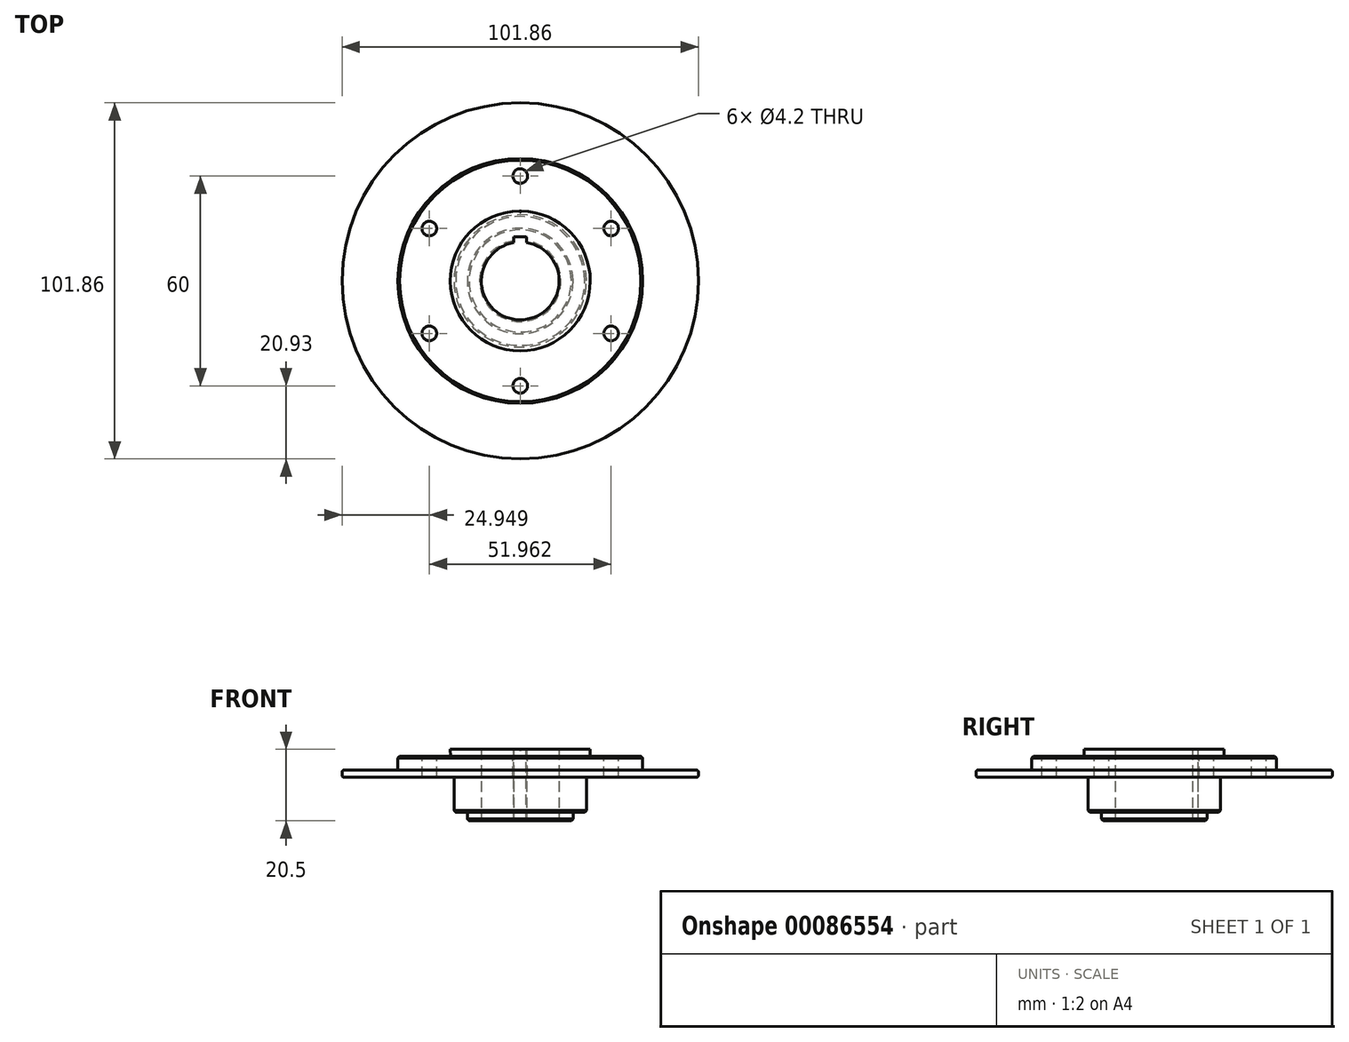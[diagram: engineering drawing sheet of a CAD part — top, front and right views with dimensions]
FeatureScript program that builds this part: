
annotation { "Feature Type Name" : "Feature", "Feature Type Description" : "" }
export const myFeature = defineFeature(function(context is Context, id is Id, definition is map)
    precondition{}
    {
        {
            var Q0;
            Q0=qCreatedBy(makeId("Front.planeOp"),FACE);
            var sketch = newSketch(context, id + "F0", { "sketchPlane" : qUnion([Q0])});
            skLineSegment(sketch, "E0", {"start": v(-11.12, -17.6) * mm, "end": v(-15.1, -17.6) * mm});
            skLineSegment(sketch, "E1", {"start": v(-15.1, -17.6) * mm, "end": v(-15.1, -15.1) * mm});
            skLineSegment(sketch, "E2", {"start": v(-15.1, -15.1) * mm, "end": v(-18.93, -15.1) * mm});
            skLineSegment(sketch, "E3", {"start": v(-18.93, -15.1) * mm, "end": v(-18.93, -5.1) * mm});
            skLineSegment(sketch, "E4", {"start": v(0, 0) * mm, "end": v(0, 28.12) * mm, "construction": true});
            skLineSegment(sketch, "E5", {"start": v(-11.12, -17.6) * mm, "end": v(-11.12, 8.2) * mm, "construction": true});
            skLineSegment(sketch, "E6", {"start": v(-35, 0.9) * mm, "end": v(-19.97, 0.9) * mm});
            skLineSegment(sketch, "E7", {"start": v(-35, 0.9) * mm, "end": v(-35, -3.1) * mm});
            skLineSegment(sketch, "E8", {"start": v(-11.12, -17.6) * mm, "end": v(-11.12, 2.9) * mm});
            skLineSegment(sketch, "E9", {"start": v(-11.13, 2.9) * mm, "end": v(-20, 2.9) * mm});
            skLineSegment(sketch, "E10", {"start": v(-20, 2.9) * mm, "end": v(-19.97, 0.9) * mm});
            skLineSegment(sketch, "E11", {"start": v(-35, -3.1) * mm, "end": v(-50.43, -3.1) * mm});
            skLineSegment(sketch, "E12", {"start": v(-50.93, -3.6) * mm, "end": v(-50.93, -4.6) * mm});
            skLineSegment(sketch, "E13", {"start": v(-50.43, -5.1) * mm, "end": v(-18.93, -5.1) * mm});
            skPoint(sketch, "E14.visualSharp", {"position": v(-50.93, -3.1) * mm});
            skArc(sketch, "E14.filletArc", {"start": v(-50.43, -3.1) * mm, "mid": v(-50.78, -3.25) * mm, "end": v(-50.93, -3.6) * mm});
            skPoint(sketch, "E15.visualSharp", {"position": v(-50.93, -5.1) * mm});
            skArc(sketch, "E15.filletArc", {"start": v(-50.93, -4.6) * mm, "mid": v(-50.78, -4.95) * mm, "end": v(-50.43, -5.1) * mm});
            skSolve(sketch);
        }
        {
            var Q0;
            Q0=makeQuery(id+"F0.imprint","IMPRINT",FACE,{"disambiguationData":[TD([[makeQuery(id+"F0.imprint","IMPRINT",EDGE,{"derivedFrom":sQuery(id+"F0.wireOp",EDGE,"E0")}),-1.0]])]});
            var Q1;
            Q1=sQuery(id+"F0.wireOp",EDGE,"E4");
            revolve(context, id + "F1", {"entities" : qUnion([Q0]), "axis" : qUnion([Q1]), "revolveType" : RevolveType.FULL});
        }
        {
            var Q0;
            Q0=makeQuery(id+"F1.opRevolve","SWEPT_EDGE",EDGE,{"disambiguationData":[OSD([sQuery(id+"F0.wireOp",EDGE,"E0"),sQuery(id+"F0.wireOp",EDGE,"E1")])]});
            var Q1;
            Q1=makeQuery(id+"F1.opRevolve","SWEPT_EDGE",EDGE,{"disambiguationData":[OSD([sQuery(id+"F0.wireOp",EDGE,"E2"),sQuery(id+"F0.wireOp",EDGE,"E3")])]});
            var Q2;
            Q2=makeQuery(id+"F1.opRevolve","SWEPT_EDGE",EDGE,{"disambiguationData":[OSD([sQuery(id+"F0.wireOp",EDGE,"E0"),sQuery(id+"F0.wireOp",EDGE,"VpWaw3KQ-EP3Q-zTOo-1TWU-8Jv2ZzNU0UUm")])]});
            var Q3;
            Q3=makeQuery(id+"F1.opRevolve","SWEPT_EDGE",EDGE,{"disambiguationData":[OSD([sQuery(id+"F0.wireOp",EDGE,"VpWaw3KQ-EP3Q-zTOo-1TWU-8Jv2ZzNU0UUm"),sQuery(id+"F0.wireOp",EDGE,"Cdg7jDaJ-U3KB-svcD-8TqX-HCB60pw5RLad")])]});
            chamfer(context, id + "F2", {"entities" : qUnion([Q0, Q1, Q2, Q3]), "width" : .5 * mm, "tangentPropagation" : true});
        }
        {
            var Q0;
            Q0=makeQuery(id+"F1.opRevolve","SWEPT_FACE",FACE,{"disambiguationData":[OSD([sQuery(id+"F0.wireOp",EDGE,"E6")])]});
            var sketch = newSketch(context, id + "F3", { "sketchPlane" : qUnion([Q0])});
            skCircle(sketch, "E16", {"center": v(0, 30) * mm, "radius": 2.1 * mm});
            skLineSegment(sketch, "E17", {"start": v(0, -1.97) * mm, "end": v(0, 19.04) * mm, "construction": true});
            skSolve(sketch);
        }
        {
            var Q0;
            Q0=makeQuery(id+"F3.imprint","IMPRINT",FACE,{"disambiguationData":[TD([[makeQuery(id+"F3.imprint","IMPRINT",EDGE,{"derivedFrom":sQuery(id+"F3.wireOp",EDGE,"E16")}),1.0]])]});
            extrude(context, id + "F4", {"entities" : qUnion([Q0]), "operationType" : NewBodyOperationType.REMOVE, "endBound" : BoundingType.UP_TO_NEXT, "oppositeDirection" : true, "depth" : 25 * mm});
        }
        {
            var Q0;
            Q0=makeQuery(id+"F4.boolean.opBoolean","COPY",FACE,{"derivedFrom":makeQuery(id+"F4.opExtrude","SWEPT_FACE",FACE,{"disambiguationData":[OSD([sQuery(id+"F3.wireOp",EDGE,"E16")])]})});
            var Q1;
            Q1=makeQuery(id+"F1.opRevolve","SWEPT_EDGE",EDGE,{"disambiguationData":[OSD([sQuery(id+"F0.wireOp",EDGE,"E8"),sQuery(id+"F0.wireOp",EDGE,"E9")])]});
            circularPattern(context, id + "F5", {"operationType" : NewBodyOperationType.REMOVE, "faces" : qUnion([Q0]), "axis" : qUnion([Q1]), "angle" : 360 * degree, "instanceCount" : 6, "equalSpace" : true, "patternType" : PatternType.FACE});
        }
        {
            var Q0;
            Q0=makeQuery(id+"F1.opRevolve","SWEPT_FACE",FACE,{"disambiguationData":[OSD([sQuery(id+"F0.wireOp",EDGE,"E9")])]});
            var sketch = newSketch(context, id + "F6", { "sketchPlane" : qUnion([Q0])});
            skLineSegment(sketch, "E18.bottom", {"start": v(1.83, 9.62) * mm, "end": v(-1.83, 9.62) * mm});
            skLineSegment(sketch, "E18.top", {"start": v(1.83, 12.62) * mm, "end": v(-1.83, 12.62) * mm});
            skLineSegment(sketch, "E18.left", {"start": v(1.83, 9.62) * mm, "end": v(1.83, 12.62) * mm});
            skLineSegment(sketch, "E18.right", {"start": v(-1.83, 9.62) * mm, "end": v(-1.83, 12.62) * mm});
            skPoint(sketch, "E18.middle", {"position": v(0, 11.12) * mm});
            skLineSegment(sketch, "E19", {"start": v(0, 0) * mm, "end": v(0, 11.12) * mm, "construction": true});
            skSolve(sketch);
        }
        {
            var Q0;
            {var subQ0=sQuery(id+"F6.wireOp",EDGE,"E18.bottom");Q0=makeQuery(id+"F6.imprint","IMPRINT",FACE,{"disambiguationData":[TD([[makeQuery(id+"F6.imprint","IMPRINT",EDGE,{"derivedFrom":subQ0}),-1.0]])]});}
            var Q1;
            {var subQ0=sQuery(id+"F6.wireOp",EDGE,"E18.top");Q1=makeQuery(id+"F6.imprint","IMPRINT",FACE,{"disambiguationData":[TD([[makeQuery(id+"F6.imprint","IMPRINT",EDGE,{"derivedFrom":subQ0}),1.0]])]});}
            extrude(context, id + "F7", {"entities" : qUnion([Q0, Q1]), "operationType" : NewBodyOperationType.REMOVE, "endBound" : BoundingType.UP_TO_NEXT, "oppositeDirection" : true, "depth" : 25 * mm});
        }
        {
            var Q0;
            Q0=makeQuery(id+"F7.boolean.opBoolean","COPY",EDGE,{"derivedFrom":makeQuery(id+"F7.opExtrude","TWEAK_EDGE",EDGE,{"derivedFrom":[makeQuery(id+"F1.opRevolve","SWEPT_FACE",FACE,{"disambiguationData":[OSD([sQuery(id+"F0.wireOp",EDGE,"E0")])]}),makeQuery(id+"F6.imprint","IMPRINT",EDGE,{"derivedFrom":sQuery(id+"F6.wireOp",EDGE,"E18.bottom")})]})});
            var Q1;
            Q1=makeQuery(id+"F7.boolean.opBoolean","COPY",EDGE,{"derivedFrom":makeQuery(id+"F7.opExtrude","SWEPT_EDGE",EDGE,{"disambiguationData":[OSD([sQuery(id+"F6.wireOp",EDGE,"E18.bottom"),sQuery(id+"F6.wireOp",EDGE,"E18.left")])]})});
            chamfer(context, id + "F8", {"entities" : qUnion([Q0, Q1]), "width" : .1 * mm, "tangentPropagation" : true});
        }
        {
            var Q0;
            Q0=makeQuery(id+"F1.opRevolve","SWEPT_EDGE",EDGE,{"disambiguationData":[OSD([sQuery(id+"F0.wireOp",EDGE,"E6"),sQuery(id+"F0.wireOp",EDGE,"E7")])]});
            chamfer(context, id + "F9", {"entities" : qUnion([Q0]), "width" : .5 * mm, "tangentPropagation" : true});
        }
        {
            var Q0;
            Q0=makeQuery(id+"F1.opRevolve","SWEPT_FACE",FACE,{"disambiguationData":[OSD([sQuery(id+"F0.wireOp",EDGE,"E9")])]});
            var sketch = newSketch(context, id + "F10", { "sketchPlane" : qUnion([Q0])});
            skCircle(sketch, "E20", {"center": v(0, 20) * mm, "radius": 0.25 * mm});
            skSolve(sketch);
        }
        {
            var Q0;
            {var subQ0=sQuery(id+"F10.wireOp",EDGE,"E20");var subQ1=makeQuery(id+"F1.opRevolve","SWEPT_EDGE",EDGE,{"disambiguationData":[OSD([sQuery(id+"F0.wireOp",EDGE,"E9"),sQuery(id+"F0.wireOp",EDGE,"E10")])]});var subQ2=makeQuery(id+"F10.imprint","INTERSECT",VERTEX,{"disambiguationData":[OD(0.0)],"derivedFrom":[subQ1,subQ0]});Q0=makeQuery(id+"F10.imprint","IMPRINT",FACE,{"disambiguationData":[TD([[makeQuery(id+"F10.imprint","IMPRINT",EDGE,{"disambiguationData":[TD([[subQ2,-1.0]])],"derivedFrom":subQ0}),1.0]])]});}
            extrude(context, id + "F11", {"entities" : qUnion([Q0]), "operationType" : NewBodyOperationType.REMOVE, "oppositeDirection" : true, "depth" : .25 * mm});
        }
    });
